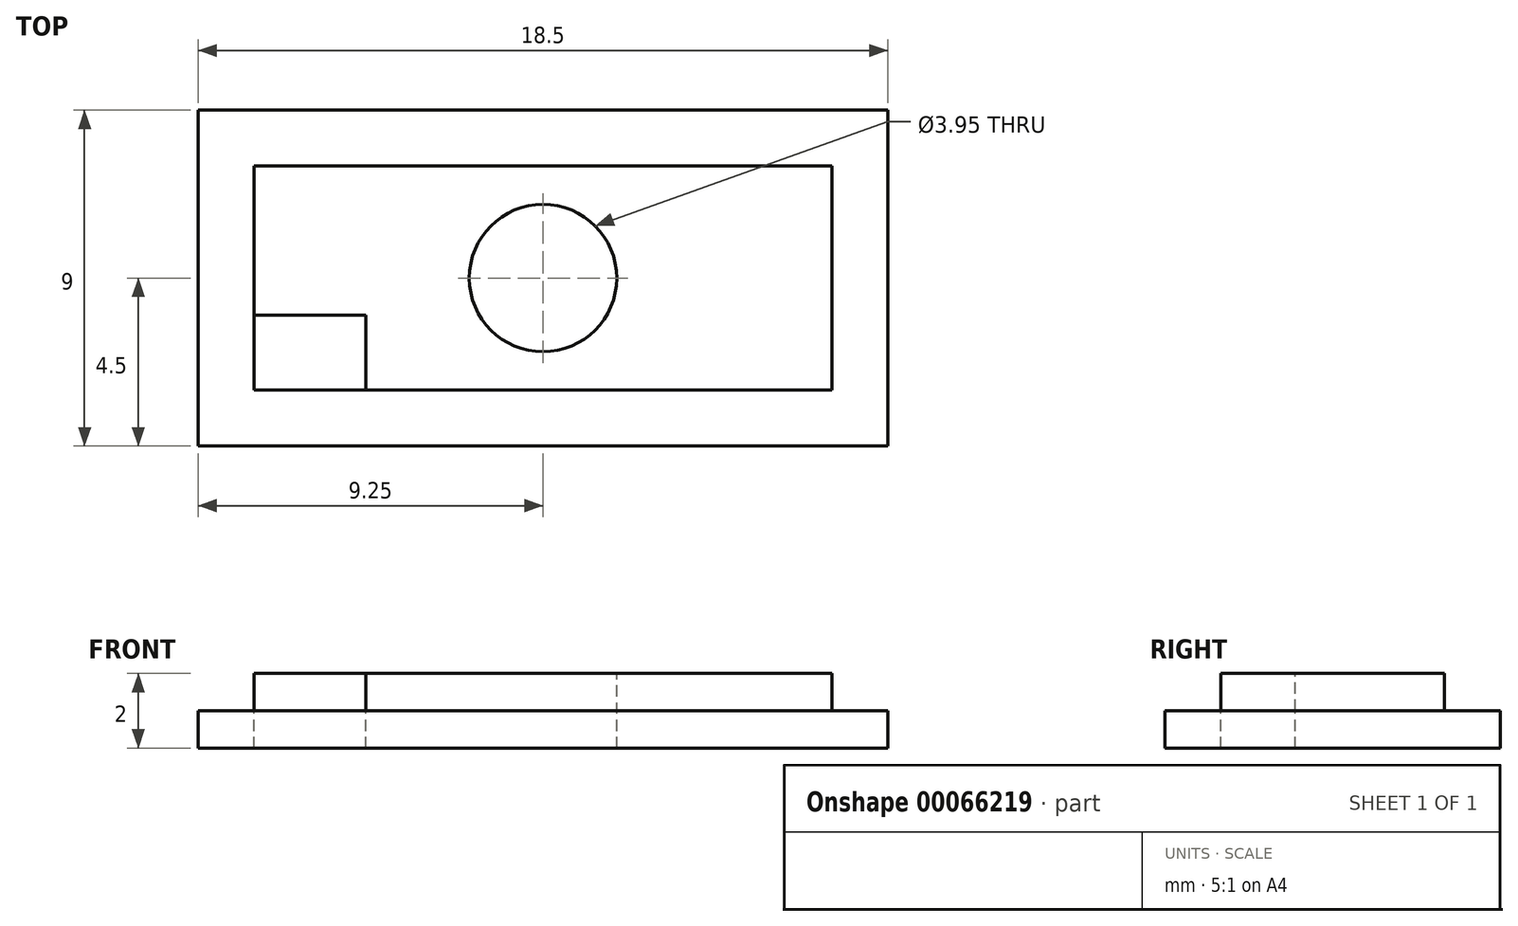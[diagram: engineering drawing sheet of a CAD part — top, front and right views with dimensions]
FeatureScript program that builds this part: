
annotation { "Feature Type Name" : "Feature", "Feature Type Description" : "" }
export const myFeature = defineFeature(function(context is Context, id is Id, definition is map)
    precondition{}
    {
        {
            var Q0;
            Q0=qCreatedBy(makeId("Top.planeOp"),FACE);
            var sketch = newSketch(context, id + "F0", { "sketchPlane" : qUnion([Q0])});
            skLineSegment(sketch, "E0.rect.bottom", {"start": v(9.25, 4.5) * mm, "end": v(-9.25, 4.5) * mm});
            skLineSegment(sketch, "E0.rect.top", {"start": v(9.25, -4.5) * mm, "end": v(-9.25, -4.5) * mm});
            skLineSegment(sketch, "E0.rect.left", {"start": v(9.25, 4.5) * mm, "end": v(9.25, -4.5) * mm});
            skLineSegment(sketch, "E0.rect.right", {"start": v(-9.25, 4.5) * mm, "end": v(-9.25, -4.5) * mm});
            skPoint(sketch, "E0.rect.middle", {"position": v(0, 0) * mm});
            skSolve(sketch);
        }
        {
            var Q0;
            Q0=qSketchRegion(id+"F0",true);
            extrude(context, id + "F1", {"entities" : qUnion([Q0]), "depth" : 1 * mm});
        }
        {
            var Q0;
            Q0=makeQuery(id+"F1.opExtrude","CAP_FACE",FACE,{"disambiguationData":[OSD([sQuery(id+"F0.wireOp",EDGE,"E0.rect.bottom"),sQuery(id+"F0.wireOp",EDGE,"E0.rect.top"),sQuery(id+"F0.wireOp",EDGE,"E0.rect.left"),sQuery(id+"F0.wireOp",EDGE,"E0.rect.right")])],"isStart":false});
            var sketch = newSketch(context, id + "F2", { "sketchPlane" : qUnion([Q0])});
            skLineSegment(sketch, "E1.rect.bottom", {"start": v(7.75, 3) * mm, "end": v(-7.75, 3) * mm});
            skLineSegment(sketch, "E1.rect.top", {"start": v(7.75, -3) * mm, "end": v(-7.75, -3) * mm});
            skLineSegment(sketch, "E1.rect.left", {"start": v(7.75, 3) * mm, "end": v(7.75, -3) * mm});
            skLineSegment(sketch, "E1.rect.right", {"start": v(-7.75, 3) * mm, "end": v(-7.75, -3) * mm});
            skPoint(sketch, "E1.rect.middle", {"position": v(0, 0) * mm});
            skSolve(sketch);
        }
        {
            var Q0;
            Q0=qSketchRegion(id+"F2",true);
            extrude(context, id + "F3", {"entities" : qUnion([Q0]), "operationType" : NewBodyOperationType.ADD, "depth" : 1 * mm});
        }
        {
            var Q0;
            Q0=makeQuery(id+"F3.opExtrude","CAP_FACE",FACE,{"disambiguationData":[OSD([sQuery(id+"F2.wireOp",EDGE,"E1.rect.bottom"),sQuery(id+"F2.wireOp",EDGE,"E1.rect.top"),sQuery(id+"F2.wireOp",EDGE,"E1.rect.left"),sQuery(id+"F2.wireOp",EDGE,"E1.rect.right")])],"isStart":false});
            var sketch = newSketch(context, id + "F4", { "sketchPlane" : qUnion([Q0])});
            skCircle(sketch, "E2", {"center": v(0, 0) * mm, "radius": 1.98 * mm});
            skLineSegment(sketch, "E3.bottom", {"start": v(-7.75, -3) * mm, "end": v(-4.75, -3) * mm});
            skLineSegment(sketch, "E3.top", {"start": v(-7.75, -1) * mm, "end": v(-4.75, -1) * mm});
            skLineSegment(sketch, "E3.left", {"start": v(-7.75, -3) * mm, "end": v(-7.75, -1) * mm});
            skLineSegment(sketch, "E3.right", {"start": v(-4.75, -3) * mm, "end": v(-4.75, -1) * mm});
            skSolve(sketch);
        }
        {
            var Q0;
            Q0=qSketchRegion(id+"F4",true);
            extrude(context, id + "F5", {"entities" : qUnion([Q0]), "operationType" : NewBodyOperationType.REMOVE, "oppositeDirection" : true, "depth" : 2 * mm});
        }
    });
